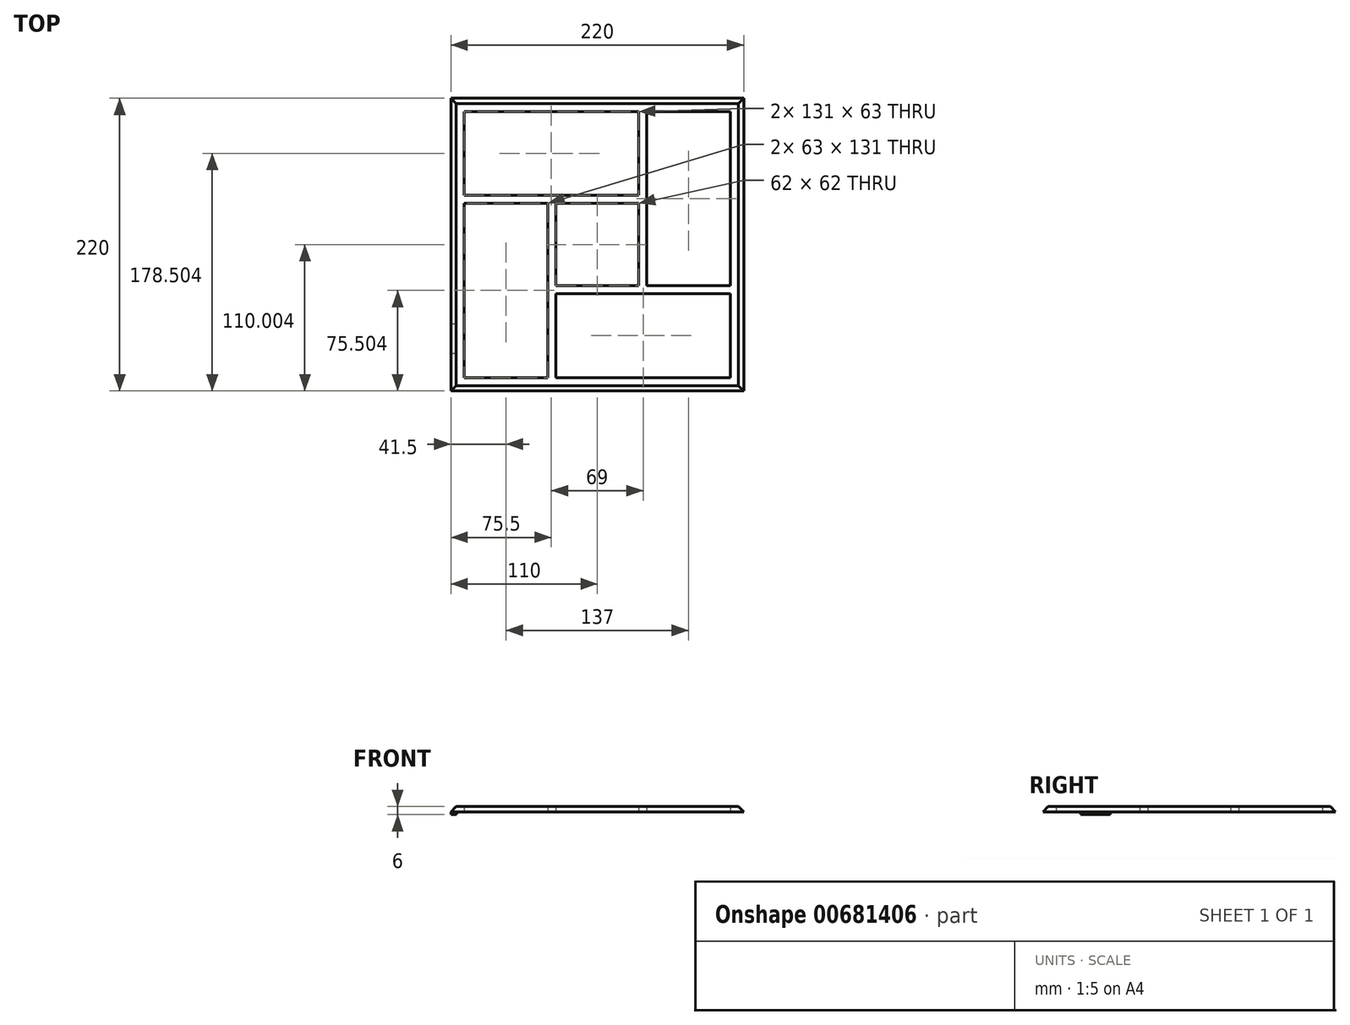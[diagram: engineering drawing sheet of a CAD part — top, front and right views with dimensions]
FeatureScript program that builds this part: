
annotation { "Feature Type Name" : "Feature", "Feature Type Description" : "" }
export const myFeature = defineFeature(function(context is Context, id is Id, definition is map)
    precondition{}
    {
        {
            var Q0;
            Q0=qCreatedBy(makeId("Top.planeOp"),FACE);
            var sketch = newSketch(context, id + "F0", { "sketchPlane" : qUnion([Q0])});
            skLineSegment(sketch, "E0.bottom", {"start": v(-100, 105.84) * mm, "end": v(31, 105.84) * mm});
            skLineSegment(sketch, "E0.top", {"start": v(-100, -94.16) * mm, "end": v(-37, -94.16) * mm});
            skLineSegment(sketch, "E0.left", {"start": v(-100, 105.84) * mm, "end": v(-100, 42.84) * mm});
            skLineSegment(sketch, "E0.right", {"start": v(100, 105.84) * mm, "end": v(100, -25.16) * mm});
            skLineSegment(sketch, "E1.0", {"start": v(-110, 115.84) * mm, "end": v(-110, -104.16) * mm});
            skLineSegment(sketch, "E1.1", {"start": v(-110, 115.84) * mm, "end": v(110, 115.84) * mm});
            skLineSegment(sketch, "E1.2", {"start": v(110, 115.84) * mm, "end": v(110, -104.16) * mm});
            skLineSegment(sketch, "E1.3", {"start": v(-110, -104.16) * mm, "end": v(110, -104.16) * mm});
            skLineSegment(sketch, "E2", {"start": v(-100, 42.84) * mm, "end": v(31, 42.84) * mm});
            skLineSegment(sketch, "E3", {"start": v(-31, -31.16) * mm, "end": v(100, -31.16) * mm});
            skLineSegment(sketch, "E4", {"start": v(-37, 36.84) * mm, "end": v(-37, -94.16) * mm});
            skLineSegment(sketch, "E5", {"start": v(37, 105.84) * mm, "end": v(37, -25.16) * mm});
            skLineSegment(sketch, "E6.0", {"start": v(-100, 36.84) * mm, "end": v(-37, 36.84) * mm});
            skLineSegment(sketch, "E7.0", {"start": v(-31, -25.16) * mm, "end": v(31, -25.16) * mm});
            skLineSegment(sketch, "E8.0", {"start": v(31, 105.84) * mm, "end": v(31, 42.84) * mm});
            skLineSegment(sketch, "E9.0", {"start": v(-31, 36.84) * mm, "end": v(-31, -25.16) * mm});
            skLineSegment(sketch, "E10.trimOffspring", {"start": v(-31, 36.84) * mm, "end": v(31, 36.84) * mm});
            skLineSegment(sketch, "E11.trimOffspring", {"start": v(31, 36.84) * mm, "end": v(31, -25.16) * mm});
            skLineSegment(sketch, "E12.trimOffspring", {"start": v(-31, -31.16) * mm, "end": v(-31, -94.16) * mm});
            skLineSegment(sketch, "E13.trimOffspring", {"start": v(37, -25.16) * mm, "end": v(100, -25.16) * mm});
            skLineSegment(sketch, "E14.trimOffspring", {"start": v(-100, 36.84) * mm, "end": v(-100, -94.16) * mm});
            skLineSegment(sketch, "E15.trimOffspring", {"start": v(100, -31.16) * mm, "end": v(100, -94.16) * mm});
            skLineSegment(sketch, "E16.trimOffspring", {"start": v(37, 105.84) * mm, "end": v(100, 105.84) * mm});
            skLineSegment(sketch, "E17.trimOffspring", {"start": v(-31, -94.16) * mm, "end": v(100, -94.16) * mm});
            skLineSegment(sketch, "E18.bottom", {"start": v(-110, -75.72) * mm, "end": v(-105.65, -75.72) * mm});
            skLineSegment(sketch, "E18.top", {"start": v(-110, -53.64) * mm, "end": v(-105.65, -53.64) * mm});
            skLineSegment(sketch, "E18.left", {"start": v(-110, -75.72) * mm, "end": v(-110, -53.64) * mm});
            skLineSegment(sketch, "E18.right", {"start": v(-105.65, -75.72) * mm, "end": v(-105.65, -53.64) * mm});
            skSolve(sketch);
        }
        {
            var Q0;
            Q0=makeQuery(id+"F0.imprint","IMPRINT",FACE,{"disambiguationData":[TD([[makeQuery(id+"F0.imprint","IMPRINT",EDGE,{"derivedFrom":sQuery(id+"F0.wireOp",EDGE,"E0.bottom")}),1.0]])]});
            extrude(context, id + "F1", {"entities" : qUnion([Q0]), "depth" : 4 * mm, "offsetDistance" : 25 * mm});
        }
        {
            var Q0;
            Q0 = qSketchRegion(id + "F0", true);
            extrude(context, id + "F2", {"entities" : qUnion([Q0]), "operationType" : NewBodyOperationType.ADD, "depth" : 4 * mm, "offsetDistance" : 25 * mm});
        }
        {
            var Q0;
            Q0=makeQuery(id+"F1.opExtrude","CAP_EDGE",EDGE,{"disambiguationData":[OSD([sQuery(id+"F0.wireOp",EDGE,"E1.3")])],"isStart":false});
            var Q1;
            Q1=makeQuery(id+"F1.opExtrude","CAP_EDGE",EDGE,{"disambiguationData":[OSD([sQuery(id+"F0.wireOp",EDGE,"E1.2")])],"isStart":false});
            var Q2;
            Q2=makeQuery(id+"F1.opExtrude","CAP_EDGE",EDGE,{"disambiguationData":[OSD([sQuery(id+"F0.wireOp",EDGE,"E1.0")])],"isStart":false});
            var Q3;
            Q3=makeQuery(id+"F1.opExtrude","CAP_EDGE",EDGE,{"disambiguationData":[OSD([sQuery(id+"F0.wireOp",EDGE,"E1.1")])],"isStart":false});
            chamfer(context, id + "F3", {"entities" : qUnion([Q0, Q1, Q2, Q3]), "width" : 4 * mm, "tangentPropagation" : true});
        }
        {
            var Q0;
            Q0=makeQuery(id+"F0.imprint","IMPRINT",FACE,{"disambiguationData":[TD([[makeQuery(id+"F0.imprint","IMPRINT",EDGE,{"derivedFrom":sQuery(id+"F0.wireOp",EDGE,"E18.bottom")}),1.0]])]});
            extrude(context, id + "F4", {"entities" : qUnion([Q0]), "operationType" : NewBodyOperationType.ADD, "oppositeDirection" : true, "depth" : 2 * mm, "offsetDistance" : 25 * mm});
        }
    });
